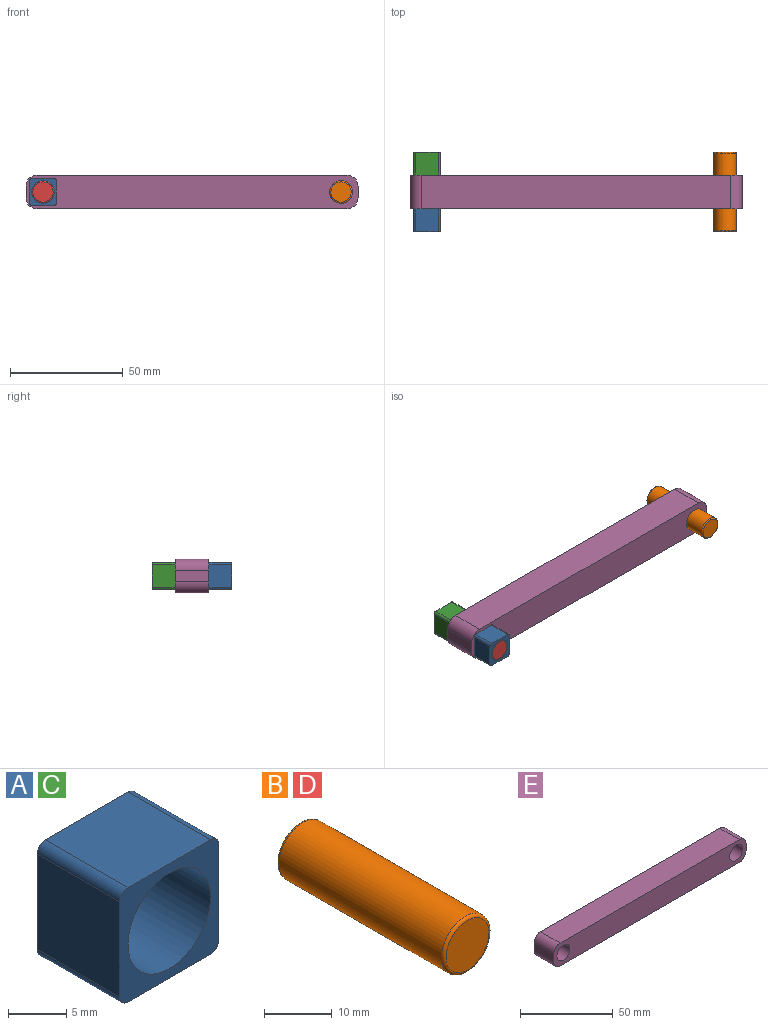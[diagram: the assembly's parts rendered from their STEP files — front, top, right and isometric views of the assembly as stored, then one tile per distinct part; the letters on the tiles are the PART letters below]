
ASSEMBLY  parts=5 mates=4
PART A: 11 faces, bbox 12x10x12 mm
  f0: plane 10x10mm, normal (1,0,0), area 100mm2, adj f5,f6,f7,f10
  f1: plane 10x10mm, normal (0,0,1), area 100mm2, adj f5,f6,f7,f8
  f2: plane 10x10mm, normal (-1,0,0), area 100mm2, adj f5,f6,f8,f9
  f3: cylinder r=5mm len=10mm, axis (0,1,0), area 314.2mm2, adj f5,f6
  f4: plane 10x10mm, normal (0,0,-1), area 100mm2, adj f5,f6,f9,f10
  f5: plane 12x12mm, normal (0,-1,0), area 64.6mm2, adj f0,f1,f2,f3,f4,f7,f8,f9
  f6: plane 12x12mm, normal (0,1,0), area 64.6mm2, adj f0,f1,f2,f3,f4,f7,f8,f9
  f7: cylinder r=1mm len=10mm, axis (0,1,0), area 15.7mm2, adj f0,f1,f5,f6
  f8: cylinder r=1mm len=10mm, axis (0,-1,0), area 15.7mm2, adj f1,f2,f5,f6
  f9: cylinder r=1mm len=10mm, axis (0,1,0), area 15.7mm2, adj f2,f4,f5,f6
  f10: cylinder r=1mm len=10mm, axis (0,-1,0), area 15.7mm2, adj f0,f4,f5,f6
PART B: 5 faces, bbox 10.8x35x10.8 mm
  f0: cylinder r=5mm len=34mm, axis (0,1,0), area 1068.1mm2, adj f3,f4
  f1: plane 9x9mm, normal (0,-1,0), area 63.6mm2, adj f4
  f2: plane 9x9mm, normal (0,1,0), area 63.6mm2, adj f3
  f3: torus R=4.5mm, axis (0,-1,0), area 23.8mm2, adj f0,f2
  f4: torus R=4.5mm, axis (0,-1,0), area 23.8mm2, adj f0,f1
PART C: same geometry as A
PART D: same geometry as B
PART E: 12 faces, bbox 147x15x15 mm
  f0: plane 137x15mm, normal (0,0,1), area 2055mm2, adj f6,f7,f8,f11
  f1: plane 15x5mm, normal (-1,0,0), area 75mm2, adj f6,f7,f8,f9
  f2: plane 137x15mm, normal (0,0,-1), area 2055mm2, adj f6,f7,f9,f10
  f3: cylinder r=5mm len=15mm, axis (0,1,0), area 471.2mm2, adj f6,f7
  f4: cylinder r=5mm len=15mm, axis (0,1,0), area 471.2mm2, adj f6,f7
  f5: plane 15x5mm, normal (1,0,0), area 75mm2, adj f6,f7,f10,f11
  f6: plane 147x15mm, normal (0,-1,0), area 2026.5mm2, adj f0,f1,f2,f3,f4,f5,f8,f9
  f7: plane 147x15mm, normal (0,1,0), area 2026.5mm2, adj f0,f1,f2,f3,f4,f5,f8,f9
  f8: cylinder r=5mm len=15mm, axis (0,1,0), area 117.8mm2, adj f0,f1,f6,f7
  f9: cylinder r=5mm len=15mm, axis (0,-1,0), area 117.8mm2, adj f1,f2,f6,f7
  f10: cylinder r=5mm len=15mm, axis (0,1,0), area 117.8mm2, adj f2,f5,f6,f7
  f11: cylinder r=5mm len=15mm, axis (0,-1,0), area 117.8mm2, adj f0,f5,f6,f7
PLACE A t=(-1.02,39.22,-20.83)mm
PLACE B t=(130.98,64.22,-20.83)mm
PLACE C t=(-1.02,64.22,-20.83)mm
PLACE D t=(-1.02,64.22,-20.83)mm
PLACE E t=(-1.02,54.22,-20.83)mm
MATE cylindrical C.f3 <-> D.f0  axis (0,1,0) through (-1.02,64.22,-20.83)mm
MATE fastened B.f0 <-> E.f3  axis (0,-1,0) through (130.98,29.22,-20.83)mm
MATE fastened D.f0 <-> E.f4  axis (0,-1,0) through (-1.02,29.22,-20.83)mm
MATE cylindrical A.f3 <-> D.f0  axis (0,-1,0) through (-1.02,29.22,-20.83)mm
